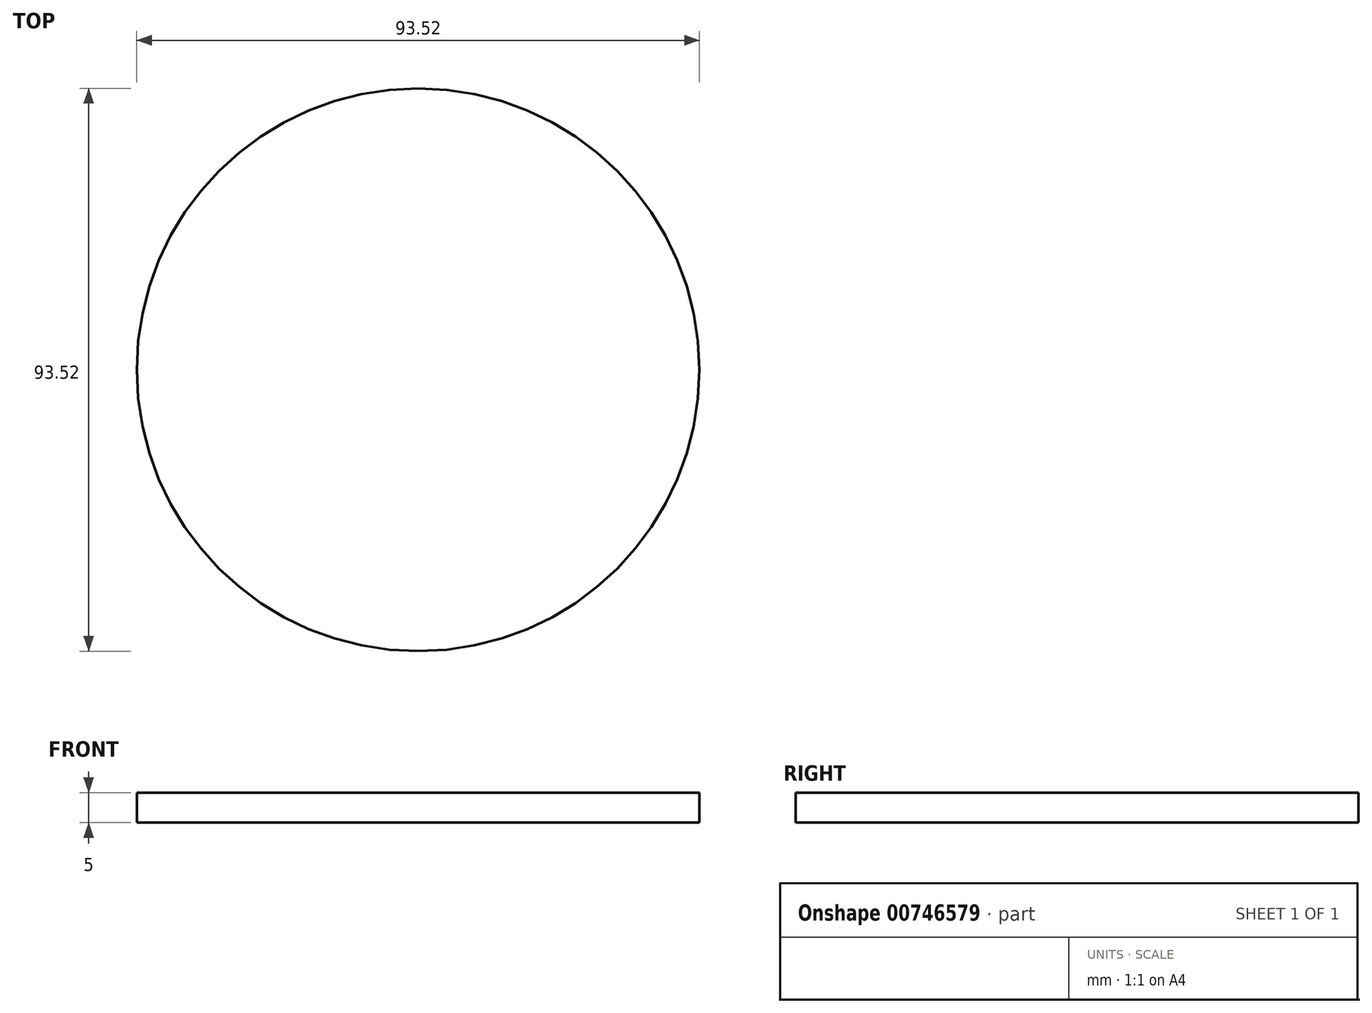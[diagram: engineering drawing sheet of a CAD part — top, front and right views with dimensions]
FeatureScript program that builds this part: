
annotation { "Feature Type Name" : "Feature", "Feature Type Description" : "" }
export const myFeature = defineFeature(function(context is Context, id is Id, definition is map)
    precondition{}
    {
        {
            var Q0;
            Q0=qCreatedBy(makeId("Top.planeOp"),FACE);
            var sketch = newSketch(context, id + "F0", { "sketchPlane" : qUnion([Q0])});
            skCircle(sketch, "E0", {"center": v(0, 0) * mm, "radius": 46.76 * mm});
            skSolve(sketch);
        }
        {
            var Q0;
            Q0 = qSketchRegion(id + "F0", true);
            extrude(context, id + "F1", {"entities" : qUnion([Q0]), "depth" : 5 * mm, "offsetDistance" : 25.4 * mm});
        }
    });
